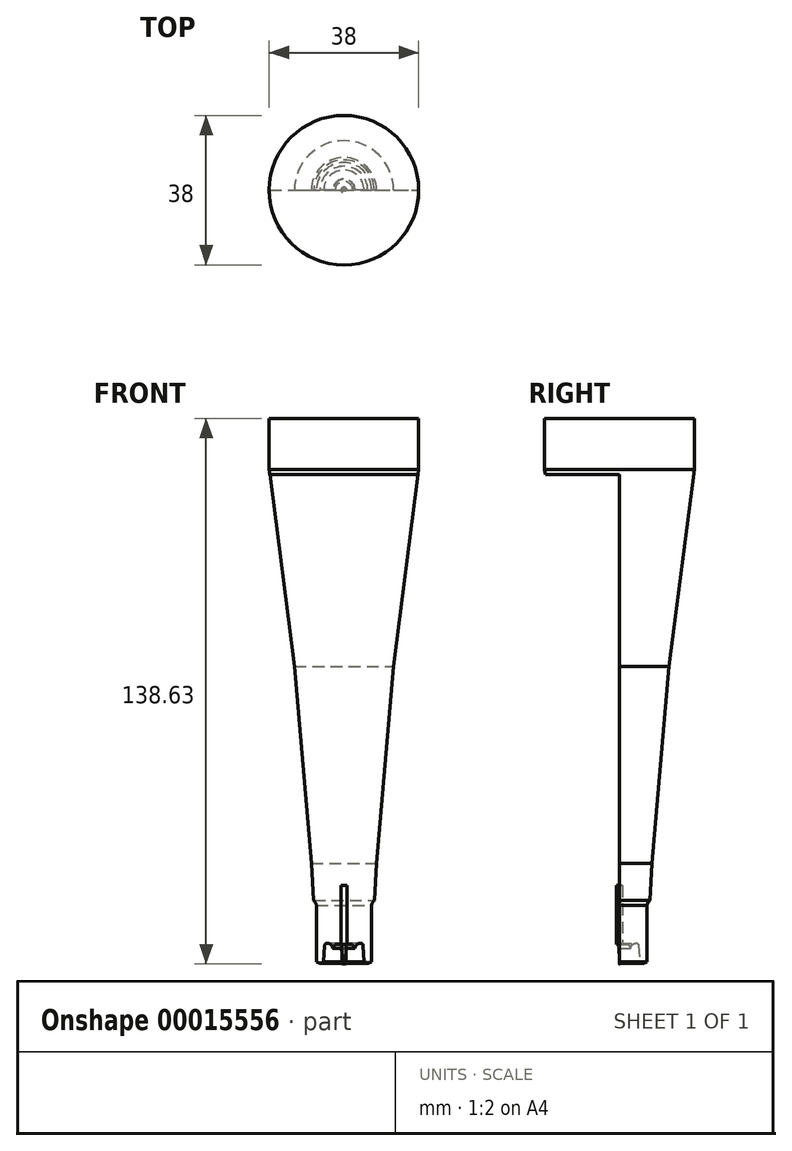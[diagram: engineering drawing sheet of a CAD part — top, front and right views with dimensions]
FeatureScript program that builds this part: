
annotation { "Feature Type Name" : "Feature", "Feature Type Description" : "" }
export const myFeature = defineFeature(function(context is Context, id is Id, definition is map)
    precondition{}
    {
        {
            var Q0;
            Q0=qCreatedBy(makeId("Front.planeOp"),FACE);
            var sketch = newSketch(context, id + "F0", { "sketchPlane" : qUnion([Q0])});
            skLineSegment(sketch, "E0", {"start": v(2.85, 0) * mm, "end": v(2.85, -3.85) * mm, "construction": true});
            skLineSegment(sketch, "E1", {"start": v(2.85, -3.85) * mm, "end": v(7, -3.85) * mm, "construction": true});
            skLineSegment(sketch, "E2", {"start": v(7, -3.85) * mm, "end": v(5.16, -3.85) * mm});
            skLineSegment(sketch, "E3", {"start": v(7, -3.85) * mm, "end": v(7, 1.65) * mm, "construction": true});
            skLineSegment(sketch, "E4", {"start": v(7, 1.65) * mm, "end": v(0, 1.65) * mm, "construction": true});
            skLineSegment(sketch, "E5", {"start": v(7, -3.85) * mm, "end": v(7, 134.65) * mm, "construction": true});
            skLineSegment(sketch, "E6", {"start": v(0, 0) * mm, "end": v(0, 150) * mm, "construction": true});
            skLineSegment(sketch, "E7", {"start": v(7, 134.65) * mm, "end": v(0, 134.65) * mm, "construction": true});
            skLineSegment(sketch, "E8", {"start": v(0, 134.65) * mm, "end": v(19, 134.65) * mm});
            skLineSegment(sketch, "E9", {"start": v(19, 134.65) * mm, "end": v(19, 121.65) * mm});
            skLineSegment(sketch, "E10", {"start": v(19, 121.65) * mm, "end": v(19, 71.65) * mm, "construction": true});
            skLineSegment(sketch, "E11", {"start": v(19, 71.65) * mm, "end": v(19, 21.65) * mm, "construction": true});
            skLineSegment(sketch, "E12", {"start": v(19, 134.65) * mm, "end": v(19, 12.15) * mm, "construction": true});
            skLineSegment(sketch, "E13", {"start": v(0, 12.15) * mm, "end": v(7.7, 12.15) * mm, "construction": true});
            skLineSegment(sketch, "E14", {"start": v(7.7, 12.15) * mm, "end": v(7.31, 12.15) * mm, "construction": true});
            skArc(sketch, "E15", {"start": v(7.7, 12.15) * mm, "mid": v(7.25, 11.62) * mm, "end": v(7, 10.97) * mm});
            skLineSegment(sketch, "E16", {"start": v(7, -3.85) * mm, "end": v(7, 10.97) * mm});
            skLineSegment(sketch, "E17", {"start": v(0, 21.65) * mm, "end": v(8.3, 21.65) * mm, "construction": true});
            skLineSegment(sketch, "E18", {"start": v(0, 71.65) * mm, "end": v(12.6, 71.65) * mm, "construction": true});
            skLineSegment(sketch, "E19", {"start": v(7.7, 12.15) * mm, "end": v(8.3, 21.65) * mm});
            skLineSegment(sketch, "E20", {"start": v(8.3, 21.65) * mm, "end": v(12.6, 71.65) * mm});
            skLineSegment(sketch, "E21", {"start": v(12.6, 71.65) * mm, "end": v(19, 121.65) * mm});
            skLineSegment(sketch, "E22", {"start": v(0, 0) * mm, "end": v(0, 134.65) * mm});
            skLineSegment(sketch, "E23", {"start": v(0, 0) * mm, "end": v(1, 0) * mm, "construction": true});
            skLineSegment(sketch, "E24", {"start": v(1, 0) * mm, "end": v(1, 1) * mm, "construction": true});
            skLineSegment(sketch, "E25", {"start": v(0, 0) * mm, "end": v(0, 1) * mm, "construction": true});
            skLineSegment(sketch, "E26", {"start": v(0, 1) * mm, "end": v(1, 1) * mm, "construction": true});
            skArc(sketch, "E27", {"start": v(1, 0) * mm, "mid": v(0.7, 0.7) * mm, "end": v(0, 1) * mm});
            skLineSegment(sketch, "E28", {"start": v(1, 0) * mm, "end": v(2.85, 0) * mm});
            skLineSegment(sketch, "E29", {"start": v(5.16, -3.85) * mm, "end": v(4.86, 1.09) * mm});
            skArc(sketch, "E30", {"start": v(4.86, 1.09) * mm, "mid": v(3.53, 1.14) * mm, "end": v(2.85, 0) * mm});
            skSolve(sketch);
        }
        {
            var Q0;
            Q0 = qSketchRegion(id + "F0", true);
            var Q1;
            Q1=sQuery(id+"F0.wireOp",EDGE,"E6");
            revolve(context, id + "F1", {"entities" : qUnion([Q0]), "axis" : qUnion([Q1]), "revolveType" : RevolveType.FULL});
        }
        {
            var Q0;
            Q0=qCreatedBy(makeId("Front.planeOp"),FACE);
            var sketch = newSketch(context, id + "F2", { "sketchPlane" : qUnion([Q0])});
            skLineSegment(sketch, "E31.bottom", {"start": v(-193.86, 120.4) * mm, "end": v(132.8, 120.4) * mm});
            skLineSegment(sketch, "E31.top", {"start": v(-193.86, -86.86) * mm, "end": v(132.8, -86.86) * mm});
            skLineSegment(sketch, "E31.left", {"start": v(-193.86, 120.4) * mm, "end": v(-193.86, -86.86) * mm});
            skLineSegment(sketch, "E31.right", {"start": v(132.8, 120.4) * mm, "end": v(132.8, -86.86) * mm});
            skSolve(sketch);
        }
        {
            var Q0;
            Q0 = qSketchRegion(id + "F2", true);
            extrude(context, id + "F3", {"entities" : qUnion([Q0]), "operationType" : NewBodyOperationType.REMOVE, "depth" : 25 * mm});
        }
        {
            var Q0;
            Q0=makeQuery(id+"F1.opRevolve","SWEPT_FACE",FACE,{"disambiguationData":[OSD([sQuery(id+"F0.wireOp",EDGE,"E28")])]});
            var sketch = newSketch(context, id + "F4", { "sketchPlane" : qUnion([Q0])});
            skCircle(sketch, "E32", {"center": v(0, 0) * mm, "radius": 2.73 * mm});
            skSolve(sketch);
        }
        {
            var Q0;
            Q0=makeQuery(id+"F1.opRevolve","SWEPT_EDGE",EDGE,{"disambiguationData":[OSD([sQuery(id+"F0.wireOp",EDGE,"E2"),sQuery(id+"F0.wireOp",EDGE,"803bf549-4cf2-41ca-b986-6d72a060b24b")])]});
            chamfer(context, id + "F5", {"entities" : qUnion([Q0]), "chamferType" : ChamferType.TWO_OFFSETS, "width1" : 1 * mm, "oppositeDirection" : false, "width2" : 0.5 * mm, "tangentPropagation" : true});
        }
        {
            var Q0;
            Q0 = qSketchRegion(id + "F4", true);
            extrude(context, id + "F6", {"entities" : qUnion([Q0]), "operationType" : NewBodyOperationType.REMOVE, "oppositeDirection" : true, "depth" : 1 * mm});
        }
        {
            var Q0;
            Q0=makeQuery(id+"F6.boolean.opBoolean","COPY",EDGE,{"derivedFrom":makeQuery(id+"F6.opExtrude","CAP_EDGE",EDGE,{"disambiguationData":[OSD([sQuery(id+"F4.wireOp",EDGE,"E32")])],"isStart":false})});
            chamfer(context, id + "F7", {"entities" : qUnion([Q0]), "chamferType" : ChamferType.TWO_OFFSETS, "width1" : .5 * mm, "oppositeDirection" : false, "width2" : 1 * mm, "tangentPropagation" : true});
        }
        {
            var Q0;
            Q0=makeQuery(id+"F1.opRevolve","SWEPT_EDGE",EDGE,{"disambiguationData":[OSD([sQuery(id+"F0.wireOp",EDGE,"E29"),sQuery(id+"F0.wireOp",EDGE,"E30")])]});
            fillet(context, id + "F8", {"entities" : qUnion([Q0]), "radius" : 0.5 * mm, "tangentPropagation" : true, "allowEdgeOverflow" : false});
        }
        {
            var Q0;
            Q0=makeQuery(id+"F6.boolean.opBoolean","COPY",FACE,{"derivedFrom":makeQuery(id+"F6.opExtrude","CAP_FACE",FACE,{"disambiguationData":[OSD([sQuery(id+"F4.wireOp",EDGE,"E32")])],"isStart":false})});
            var sketch = newSketch(context, id + "F9", { "sketchPlane" : qUnion([Q0])});
            skLineSegment(sketch, "E33.bottom", {"start": v(0.57, -0.1) * mm, "end": v(-0.57, -0.1) * mm});
            skLineSegment(sketch, "E33.top", {"start": v(0.57, 0.1) * mm, "end": v(-0.58, 0.1) * mm});
            skLineSegment(sketch, "E33.left", {"start": v(0.57, -0.1) * mm, "end": v(0.57, 0.1) * mm});
            skLineSegment(sketch, "E33.right", {"start": v(-0.57, -0.1) * mm, "end": v(-0.57, 0.1) * mm});
            skPoint(sketch, "E33.middle", {"position": v(0, 0) * mm});
            skSolve(sketch);
        }
        {
            var Q0;
            Q0 = qSketchRegion(id + "F9", true);
            extrude(context, id + "F10", {"entities" : qUnion([Q0]), "depth" : 5 * mm, "offsetDistance" : 25 * mm, "hasDraft" : true, "draftAngle" : 0.8 * degree, "draftPullDirection" : true});
        }
        {
            var Q0;
            Q0=makeQuery(id+"F10.opExtrude","CAP_EDGE",EDGE,{"disambiguationData":[OSD([sQuery(id+"F9.wireOp",EDGE,"E33.right")])],"isStart":false});
            var Q1;
            Q1=makeQuery(id+"F10.opExtrude","CAP_EDGE",EDGE,{"disambiguationData":[OSD([sQuery(id+"F9.wireOp",EDGE,"E33.left")])],"isStart":false});
            fillet(context, id + "F11", {"entities" : qUnion([Q0, Q1]), "tangentPropagation" : true, "radius" : 0.2 * mm, "defaultsChanged" : true, "vertexSettings" : [], "allowEdgeOverflow" : false});
        }
        {
            var Q0;
            Q0=makeQuery(id+"F11.opFillet","BLEND_EDGE",EDGE,{"blendedFrom":[makeQuery(id+"F10.opExtrude","CAP_EDGE",EDGE,{"disambiguationData":[OSD([sQuery(id+"F9.wireOp",EDGE,"E33.right")])],"isStart":false}),makeQuery(id+"F10.opExtrude","SWEPT_FACE",FACE,{"disambiguationData":[OSD([sQuery(id+"F9.wireOp",EDGE,"E33.top")])]})],"blendedInto":[makeQuery(id+"F10.opExtrude","SWEPT_FACE",FACE,{"disambiguationData":[OSD([sQuery(id+"F9.wireOp",EDGE,"E33.top")])]})]});
            var Q1;
            Q1=makeQuery(id+"F11.opFillet","BLEND_EDGE",EDGE,{"blendedFrom":[makeQuery(id+"F10.opExtrude","CAP_EDGE",EDGE,{"disambiguationData":[OSD([sQuery(id+"F9.wireOp",EDGE,"E33.right")])],"isStart":false}),makeQuery(id+"F10.opExtrude","SWEPT_FACE",FACE,{"disambiguationData":[OSD([sQuery(id+"F9.wireOp",EDGE,"E33.bottom")])]})],"blendedInto":[makeQuery(id+"F10.opExtrude","SWEPT_FACE",FACE,{"disambiguationData":[OSD([sQuery(id+"F9.wireOp",EDGE,"E33.bottom")])]})]});
            var Q2;
            Q2=makeQuery(id+"F10.opExtrude","CAP_EDGE",EDGE,{"disambiguationData":[OSD([sQuery(id+"F9.wireOp",EDGE,"E33.bottom")])],"isStart":false});
            var Q3;
            Q3=makeQuery(id+"F10.opExtrude","CAP_EDGE",EDGE,{"disambiguationData":[OSD([sQuery(id+"F9.wireOp",EDGE,"E33.top")])],"isStart":false});
            var Q4;
            Q4=makeQuery(id+"F11.opFillet","BLEND_EDGE",EDGE,{"blendedFrom":[makeQuery(id+"F10.opExtrude","CAP_EDGE",EDGE,{"disambiguationData":[OSD([sQuery(id+"F9.wireOp",EDGE,"E33.left")])],"isStart":false}),makeQuery(id+"F10.opExtrude","SWEPT_FACE",FACE,{"disambiguationData":[OSD([sQuery(id+"F9.wireOp",EDGE,"E33.top")])]})],"blendedInto":[makeQuery(id+"F10.opExtrude","SWEPT_FACE",FACE,{"disambiguationData":[OSD([sQuery(id+"F9.wireOp",EDGE,"E33.top")])]})]});
            var Q5;
            Q5=makeQuery(id+"F11.opFillet","BLEND_EDGE",EDGE,{"blendedFrom":[makeQuery(id+"F10.opExtrude","CAP_EDGE",EDGE,{"disambiguationData":[OSD([sQuery(id+"F9.wireOp",EDGE,"E33.left")])],"isStart":false}),makeQuery(id+"F10.opExtrude","SWEPT_FACE",FACE,{"disambiguationData":[OSD([sQuery(id+"F9.wireOp",EDGE,"E33.bottom")])]})],"blendedInto":[makeQuery(id+"F10.opExtrude","SWEPT_FACE",FACE,{"disambiguationData":[OSD([sQuery(id+"F9.wireOp",EDGE,"E33.bottom")])]})]});
            chamfer(context, id + "F12", {"entities" : qUnion([Q0, Q1, Q2, Q3, Q4, Q5]), "width" : 0.05 * mm, "tangentPropagation" : true});
        }
        {
            var Q0;
            Q0=makeQuery(id+"F10.opExtrude","CAP_FACE",FACE,{"disambiguationData":[OSD([sQuery(id+"F9.wireOp",EDGE,"E33.bottom"),sQuery(id+"F9.wireOp",EDGE,"E33.top"),sQuery(id+"F9.wireOp",EDGE,"E33.left"),sQuery(id+"F9.wireOp",EDGE,"E33.right")])],"isStart":true});
            var sketch = newSketch(context, id + "F13", { "sketchPlane" : qUnion([Q0])});
            skCircle(sketch, "E34", {"center": v(0, 0) * mm, "radius": 0.75 * mm});
            skSolve(sketch);
        }
        {
            var Q0;
            Q0 = qSketchRegion(id + "F13", true);
            extrude(context, id + "F14", {"entities" : qUnion([Q0]), "depth" : 15 * mm, "offsetDistance" : 25 * mm});
        }
        {
            var Q0;
            Q0=makeQuery(id+"F14.opExtrude","SWEPT_BODY",BODY,{"disambiguationData":[OSD([sQuery(id+"F13.wireOp",EDGE,"E34")])]});
            var Q1;
            Q1=makeQuery(id+"F1.opRevolve","SWEPT_BODY",BODY,{"disambiguationData":[OSD([sQuery(id+"F0.wireOp",EDGE,"E2"),sQuery(id+"F0.wireOp",EDGE,"E8"),sQuery(id+"F0.wireOp",EDGE,"E9"),sQuery(id+"F0.wireOp",EDGE,"E15"),sQuery(id+"F0.wireOp",EDGE,"E16"),sQuery(id+"F0.wireOp",EDGE,"E19"),sQuery(id+"F0.wireOp",EDGE,"E20"),sQuery(id+"F0.wireOp",EDGE,"E21"),sQuery(id+"F0.wireOp",EDGE,"E22"),sQuery(id+"F0.wireOp",EDGE,"E27"),sQuery(id+"F0.wireOp",EDGE,"E28"),sQuery(id+"F0.wireOp",EDGE,"E29"),sQuery(id+"F0.wireOp",EDGE,"E30")])]});
            booleanBodies(context, id + "F15", {"operationType" : BooleanOperationType.SUBTRACTION, "tools" : qUnion([Q0]), "targets" : qUnion([Q1]), "keepTools" : true});
        }
    });
